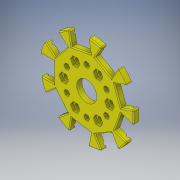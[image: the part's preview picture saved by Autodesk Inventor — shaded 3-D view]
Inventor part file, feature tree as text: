
AUTODESK INVENTOR PART (.ipt)
format: ipt  version: 2016 (Build 200138000, 138)  size: 664,576 bytes
history: native  units: in
note: dims shown in document units (in); Inventor stores cm internally (conversion verified against a paired STEP export)
features: extrude x22, sketch x22, fillet x1
ambient origin geometry x8: Origin, YZ Plane, XZ Plane, XY Plane, X Axis, Y Axis, Z Axis, Center Point
bodies: Solid1 (feature_tree)
feature tree (45):
  extrude  "Extrusion1"  Depth=1.7461in
  extrude  "Extrusion2"  Depth=0.3937in
  extrude  "Extrusion3"  Depth=0.3937in
  extrude  "Extrusion4"  Depth=0.3937in
  extrude  "Extrusion5"  Depth=0.3937in
  extrude  "Extrusion6"  Depth=0.3937in
  extrude  "Extrusion7"  Depth=0.3937in
  extrude  "Extrusion8"  Depth=0.3937in
  extrude  "Extrusion9"  Depth=0.3937in
  extrude  "Extrusion10"  Depth=0.3937in
  extrude  "Extrusion11"  Depth=0.3937in
  extrude  "Extrusion12"  Depth=0.3937in
  extrude  "Extrusion13"  Depth=0.3937in
  extrude  "Extrusion14"  Depth=0.3937in
  extrude  "Extrusion15"  Depth=0.3937in
  extrude  "Extrusion16"  Depth=0.3937in
  extrude  "Extrusion17"  Depth=0.3937in
  extrude  "Extrusion18"  Depth=0.3937in
  extrude  "Extrusion19"  Depth=0.3937in
  extrude  "Extrusion20"  Depth=0.3937in
  extrude  "Extrusion21"  Depth=0.3937in
  extrude  "Extrusion22"  Depth=0.3937in
  fillet  "Fillet1"  Radius=0.3937in
  sketch  "Sketch1"  dims[d0=3.8583in d13=1.7461in]
  sketch  "Sketch2"  dims[d14=0.3937in d16=0.3937in]
  sketch  "Sketch3"  dims[d17=0.3937in d19=1.7461in]
  sketch  "Sketch4"  dims[d20=0.1374in d21=0.3937in]
  sketch  "Sketch5"  dims[d22=0.3937in d23=1.7461in]
  sketch  "Sketch6"  dims[d24=60.0deg d25=0.3937in]
  sketch  "Sketch7"  dims[d26=0.3937in d27=1.7461in]
  sketch  "Sketch8"  dims[d28=0.6871in d29=0.3937in]
  sketch  "Sketch9"  dims[d30=0.3937in d31=1.7461in]
  sketch  "Sketch10"  dims[d32=0.962in d33=0.3937in]
  sketch  "Sketch11"  dims[d34=0.3937in d35=1.7461in]
  sketch  "Sketch12"  dims[d36=0.1374in d37=0.3937in]
  sketch  "Sketch13"  dims[d38=0.3937in d39=1.7461in]
  sketch  "Sketch14"  dims[d40=60.0deg d41=0.3937in]
  sketch  "Sketch15"  dims[d42=0.3937in d43=1.7461in]
  sketch  "Sketch16"  dims[d44=0.6871in d45=0.3937in]
  sketch  "Sketch17"  dims[d46=0.3937in d47=1.7461in]
  sketch  "Sketch18"  dims[d48=0.962in d49=0.3937in]
  sketch  "Sketch19"  dims[d50=0.3937in d51=0.3937in]
  sketch  "Sketch20"  dims[d52=0.3937in d53=0.3937in]
  sketch  "Sketch21"  dims[d54=0.3937in d55=0.3937in]
  sketch  "Sketch22"  dims[d56=0.3937in d57=0.3937in d58=0.3937in d59=0.3937in d60=0.3937in d61=0.3937in d62=0.3937in d63=0.3937in d64=0.3937in d65=0.3937in d66=0.3937in d67=0.2165in d68=0.0in d69=0.122in d70=0.1575in d71=0.0787in d72=0.0in d73=0.122in d74=0.1575in d75=0.0787in d76=0.0in d77=0.122in d78=0.1575in d79=0.0787in d80=0.0in d82=0.122in d83=0.1575in d84=0.0787in d85=0.0in d86=0.122in d87=0.1575in d88=0.0787in d89=0.0in d90=0.122in d91=0.1575in d92=0.0787in d93=0.0in d94=0.122in d95=0.1575in d96=0.0787in d97=0.0in d98=0.122in d99=0.1575in d100=0.0787in d101=0.0in d102=0.122in d103=0.1575in d104=0.0787in d105=0.0in d106=0.122in d107=0.1575in d108=0.0787in d109=0.0in d110=0.122in d111=0.1575in d112=0.0787in d113=0.0in d114=0.122in d115=0.1575in d116=0.0787in d117=0.0in d118=0.122in d119=0.1575in d120=0.0787in d121=0.0in d122=0.122in d123=0.1575in d124=0.0787in d125=0.0in d126=0.122in d127=0.1575in d128=0.0787in d129=0.0in d130=0.122in d131=0.1575in d132=0.0787in d133=0.0in d134=0.122in d135=0.1575in d136=0.0787in d137=0.0in d138=0.122in d139=0.1575in d140=0.0787in d141=0.0in d142=0.939in d143=0.939in d144=60.0deg d145=0.939in d146=120.0deg d147=0.939in d148=0.939in d149=60.0deg d150=0.939in d151=120.0deg d152=0.939in d153=30.0deg d154=0.939in d155=90.0deg d156=0.939in d157=150.0deg d158=0.939in d159=30.0deg d160=0.939in d161=90.0deg d162=0.939in d163=150.0deg d164=0.1969in d165=0.1181in d168=0.1969in d169=0.1181in d170=0.1969in d171=0.1181in d172=0.1969in d173=0.1181in d174=0.1969in d176=0.1181in d177=0.1181in d178=0.1969in d179=0.1083in d180=0.0in d181=0.939in d182=30.0deg d183=0.939in d184=60.0deg d185=0.939in d186=90.0deg d187=0.939in d188=120.0deg d189=0.939in d190=150.0deg d191=0.939in d192=180.0deg d193=0.939in d194=0.939in d195=30.0deg d196=0.939in d197=60.0deg d198=0.939in d199=90.0deg d200=0.939in d201=120.0deg d202=0.939in d203=150.0deg d204=0.1969in d205=0.1181in d206=0.1969in d207=0.1181in d208=0.1969in d209=0.1181in d210=0.1969in d211=0.1181in d212=0.1969in d213=0.1181in d214=0.1969in d215=0.1181in d216=0.1083in d217=0.0in d218=0.8268in d219=0.2165in d220=0.0in d221=0.0394in]
